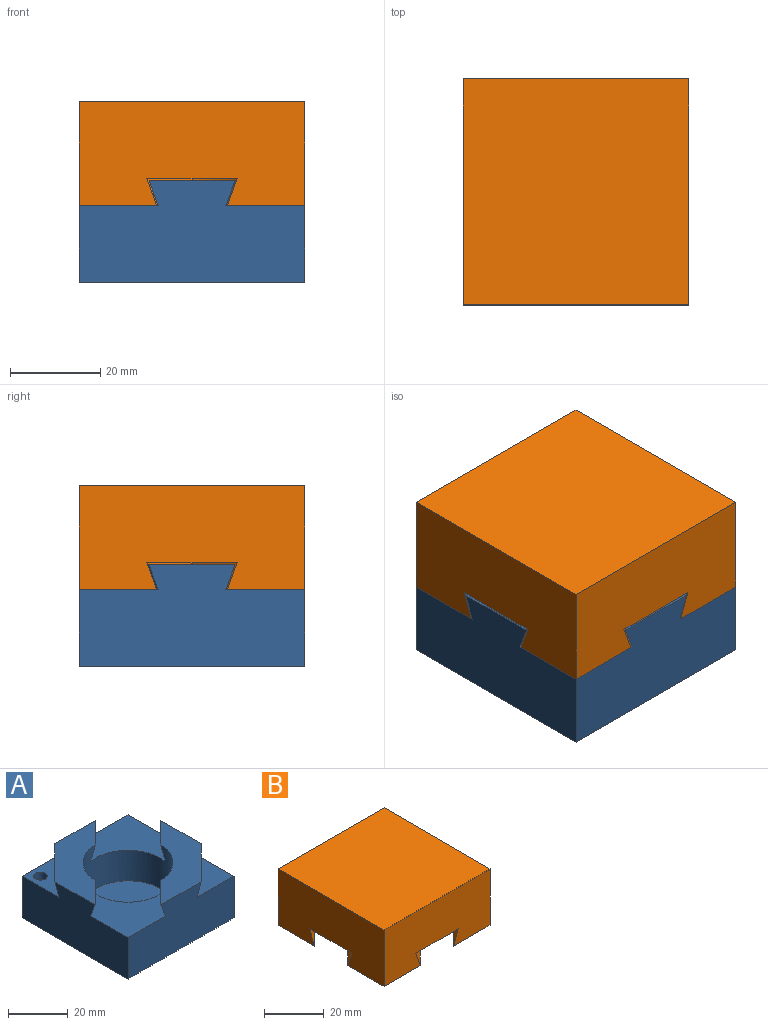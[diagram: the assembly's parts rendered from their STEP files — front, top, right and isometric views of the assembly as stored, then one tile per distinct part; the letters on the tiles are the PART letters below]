
ASSEMBLY  parts=2 mates=1
PART A: 21 faces, bbox 50x50x22.5 mm
  f0: plane 12.26x10.26mm, normal (-0.68,0.68,-0.25), area 81.1mm2, adj f5,f10,f13,f17
  f1: plane 27.76x27.76mm, normal (0,0,1), area 398.7mm2, adj f4,f7,f9,f14,f17
  f2: plane 12.26x10.26mm, normal (0.68,-0.68,-0.25), area 81.1mm2, adj f3,f6,f13,f17
  f3: plane 34.5x34.5mm, normal (0,0,1), area 418.2mm2, adj f2,f6,f7,f14,f16,f17
  f4: plane 50x22.5mm, normal (0,-1,0), area 943.5mm2, adj f1,f5,f7,f8,f9,f10,f11,f12
  f5: plane 50x22.5mm, normal (1,0,0), area 943.5mm2, adj f0,f4,f6,f8,f10,f11,f12,f13
  f6: plane 50x22.5mm, normal (0,1,0), area 943.5mm2, adj f2,f3,f5,f7,f8,f13,f15,f16
  f7: plane 50x22.5mm, normal (-1,0,0), area 943.5mm2, adj f1,f3,f4,f6,f8,f14,f15,f16
  f8: plane 50x50mm, normal (0,0,-1), area 2500mm2, adj f4,f5,f6,f7
  f9: plane 12.26x10.26mm, normal (-0.68,0.68,-0.25), area 81.1mm2, adj f1,f4,f10,f17
  f10: plane 34.5x34.5mm, normal (0,0,1), area 418.2mm2, adj f0,f4,f5,f9,f11,f17
  f11: plane 17.5x17.5mm, normal (0.68,-0.68,-0.25), area 132.5mm2, adj f4,f5,f10,f12
  f12: plane 17.5x17.5mm, normal (0,0,1), area 153.2mm2, adj f4,f5,f11
  f13: plane 27.76x27.76mm, normal (0,0,1), area 398.7mm2, adj f0,f2,f5,f6,f17
  f14: plane 12.26x10.26mm, normal (0.68,-0.68,-0.25), area 81.1mm2, adj f1,f3,f7,f17
  f15: plane 17.5x17.5mm, normal (0,0,1), area 137.3mm2, adj f6,f7,f16,f19
  f16: plane 17.5x17.5mm, normal (-0.68,0.68,-0.25), area 132.5mm2, adj f3,f6,f7,f15
  f17: cylinder r=15mm len=30mm, axis (0,0,1), area 1402mm2, adj f0,f1,f2,f3,f9,f10,f13,f14
  f18: plane 30x30mm, normal (0,0,1), area 706.9mm2, adj f17
  f19: cylinder r=2.25mm len=4.5mm, axis (0,0,1), area 42.4mm2, adj f15,f20
  f20: plane 4.5x4.5mm, normal (0,0,1), area 15.9mm2, adj f19
PART B: 22 faces, bbox 50x50x23 mm
  f0: plane 12.37x10.19mm, normal (0.68,-0.68,0.25), area 88.1mm2, adj f2,f6,f11,f19
  f1: plane 27.37x27.37mm, normal (0,0,-1), area 392.2mm2, adj f4,f7,f12,f13,f19
  f2: plane 27.37x27.37mm, normal (0,0,-1), area 392.2mm2, adj f0,f3,f5,f6,f19,f20
  f3: plane 12.37x10.19mm, normal (-0.68,0.68,0.25), area 88.1mm2, adj f2,f5,f14,f20
  f4: plane 50x23mm, normal (0,1,0), area 1043.1mm2, adj f1,f5,f7,f8,f13,f14,f15,f16
  f5: plane 50x23mm, normal (-1,0,0), area 1043.1mm2, adj f2,f3,f4,f6,f8,f14,f15,f16
  f6: plane 50x23mm, normal (0,-1,0), area 1043.1mm2, adj f0,f2,f5,f7,f8,f9,f10,f11
  f7: plane 50x23mm, normal (1,0,0), area 1043.1mm2, adj f1,f4,f6,f8,f9,f10,f11,f12
  f8: plane 50x50mm, normal (0,0,1), area 2500mm2, adj f4,f5,f6,f7
  f9: plane 17.18x17.18mm, normal (0,0,-1), area 147.6mm2, adj f6,f7,f10
  f10: plane 17.18x17.18mm, normal (-0.68,0.68,0.25), area 141mm2, adj f6,f7,f9,f11
  f11: plane 35x35mm, normal (0,0,-1), area 435.8mm2, adj f0,f6,f7,f10,f12,f19
  f12: plane 12.37x10.19mm, normal (0.68,-0.68,0.25), area 88.1mm2, adj f1,f7,f11,f19
  f13: plane 12.37x10.19mm, normal (-0.68,0.68,0.25), area 88.1mm2, adj f1,f4,f14,f19
  f14: plane 35x35mm, normal (0,0,-1), area 435.8mm2, adj f3,f4,f5,f13,f15,f19
  f15: plane 17.18x17.18mm, normal (0.68,-0.68,0.25), area 141mm2, adj f4,f5,f14,f16
  f16: plane 17.18x17.18mm, normal (0,0,-1), area 131.7mm2, adj f4,f5,f15,f17
  f17: cylinder r=2.25mm len=8mm, axis (0,0,-1), area 113.1mm2, adj f16,f18
  f18: plane 4.5x4.5mm, normal (0,0,-1), area 15.9mm2, adj f17
  f19: cylinder r=15mm len=30mm, axis (0,0,-1), area 1434.5mm2, adj f0,f1,f2,f11,f12,f13,f14,f20
  f20: cylinder r=15mm len=6mm, axis (0,0,-1), area 6.9mm2, adj f2,f3,f19
  f21: plane 30x30mm, normal (0,0,-1), area 706.9mm2, adj f19
PLACE A t=(-2.03,-2.5,15.38)mm
PLACE B t=(-2.03,-2.5,15.38)mm
MATE fastened A.f17 <-> B.f19  axis (0,0,1) through (22.97,-27.5,37.88)mm
